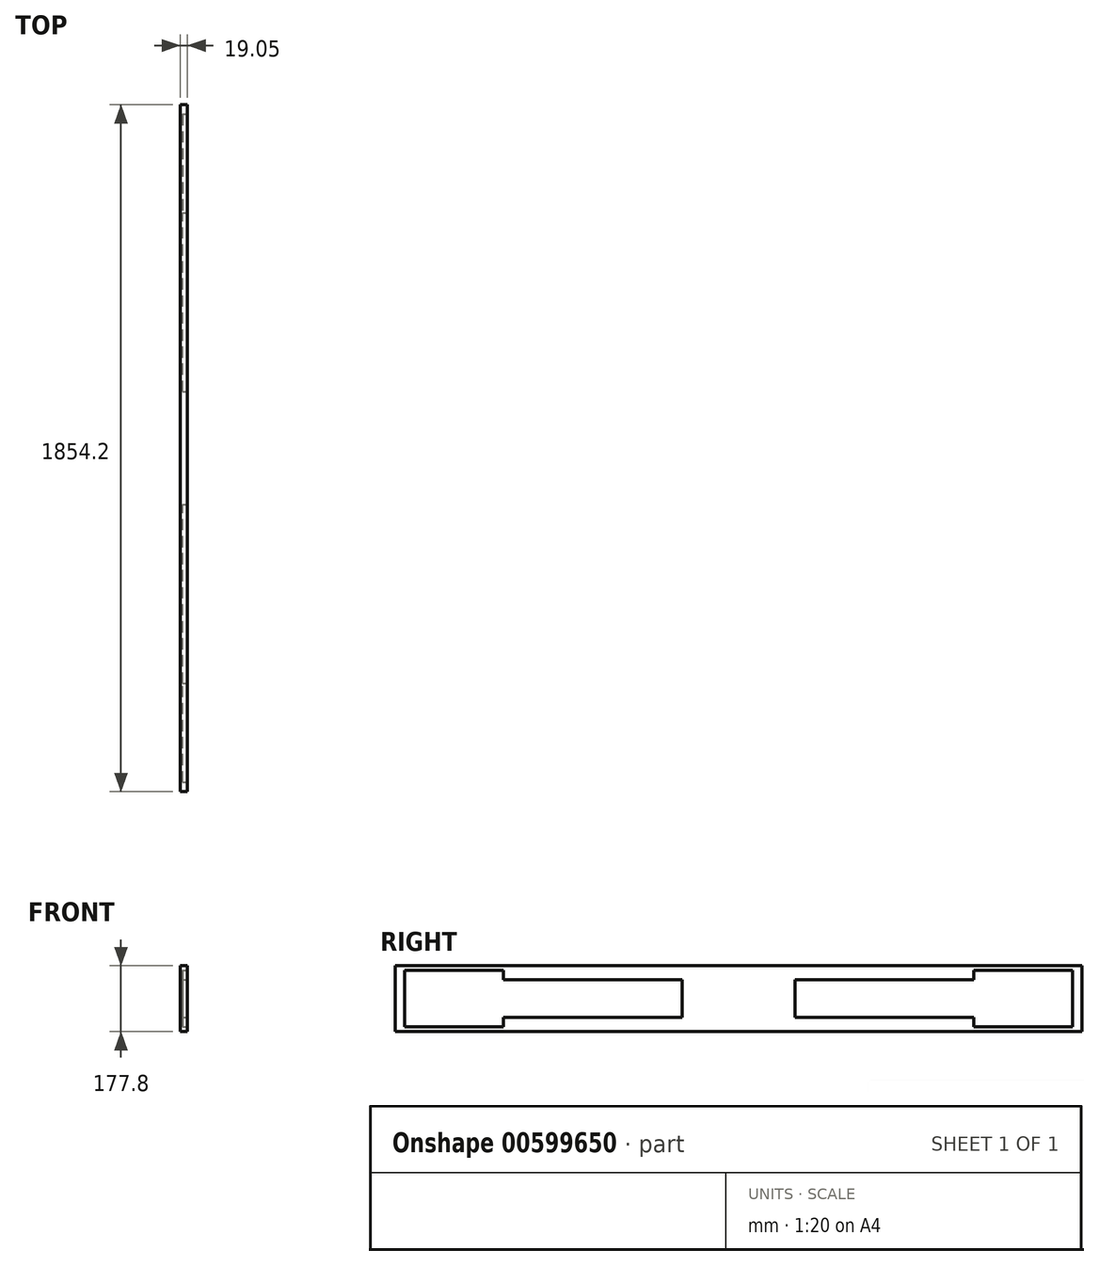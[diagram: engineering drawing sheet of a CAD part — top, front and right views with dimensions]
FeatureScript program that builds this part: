
annotation { "Feature Type Name" : "Feature", "Feature Type Description" : "" }
export const myFeature = defineFeature(function(context is Context, id is Id, definition is map)
    precondition{}
    {
        {
            var Q0;
            Q0=qCreatedBy(makeId("Front.planeOp"),FACE);
            var sketch = newSketch(context, id + "F0", { "sketchPlane" : qUnion([Q0])});
            skLineSegment(sketch, "E0.bottom", {"start": v(0, 0) * mm, "end": v(19.05, 0) * mm});
            skLineSegment(sketch, "E0.top", {"start": v(0, 177.8) * mm, "end": v(19.05, 177.8) * mm});
            skLineSegment(sketch, "E0.left", {"start": v(0, 0) * mm, "end": v(0, 177.8) * mm});
            skLineSegment(sketch, "E0.right", {"start": v(19.05, 0) * mm, "end": v(19.05, 177.8) * mm});
            skSolve(sketch);
        }
        {
            var Q0;
            Q0 = qSketchRegion(id + "F0", true);
            extrude(context, id + "F1", {"entities" : qUnion([Q0]), "endBound" : BoundingType.SYMMETRIC, "depth" : 1854.2 * mm, "offsetDistance" : 25.4 * mm});
        }
        {
            var Q0;
            Q0=makeQuery(id+"F1.opExtrude","SWEPT_FACE",FACE,{"disambiguationData":[OSD([sQuery(id+"F0.wireOp",EDGE,"E0.right")])]});
            var sketch = newSketch(context, id + "F2", { "sketchPlane" : qUnion([Q0])});
            skLineSegment(sketch, "E1", {"start": v(0, 0) * mm, "end": v(0, 177.8) * mm, "construction": true});
            skLineSegment(sketch, "E2.bottom", {"start": v(-901.7, 12.7) * mm, "end": v(-635, 12.7) * mm});
            skLineSegment(sketch, "E2.top", {"start": v(-901.7, 165.1) * mm, "end": v(-635, 165.1) * mm});
            skLineSegment(sketch, "E2.right", {"start": v(-635, 12.7) * mm, "end": v(-635, 38.1) * mm});
            skLineSegment(sketch, "E3", {"start": v(-901.7, 165.1) * mm, "end": v(-901.7, 12.7) * mm});
            skLineSegment(sketch, "E4.MirrorCS", {"start": v(901.7, 165.1) * mm, "end": v(635, 165.1) * mm});
            skLineSegment(sketch, "E5.MirrorCS", {"start": v(901.7, 12.7) * mm, "end": v(635, 12.7) * mm});
            skLineSegment(sketch, "E6.MirrorCS", {"start": v(901.7, 165.1) * mm, "end": v(901.7, 12.7) * mm});
            skLineSegment(sketch, "E7", {"start": v(-635, 139.7) * mm, "end": v(-152.4, 139.7) * mm});
            skLineSegment(sketch, "E8", {"start": v(-635, 38.1) * mm, "end": v(-152.4, 38.1) * mm});
            skLineSegment(sketch, "E9.trimOffspring", {"start": v(-635, 139.7) * mm, "end": v(-635, 165.1) * mm});
            skLineSegment(sketch, "E10.trimOffspring", {"start": v(635, 139.7) * mm, "end": v(635, 165.1) * mm});
            skLineSegment(sketch, "E11", {"start": v(635, 38.1) * mm, "end": v(635, 12.7) * mm});
            skLineSegment(sketch, "E12", {"start": v(-152.4, 139.7) * mm, "end": v(-152.4, 38.1) * mm});
            skLineSegment(sketch, "E13.MirrorCS", {"start": v(152.4, 139.7) * mm, "end": v(152.4, 38.1) * mm});
            skLineSegment(sketch, "E14.trimOffspring", {"start": v(152.4, 139.7) * mm, "end": v(635, 139.7) * mm});
            skLineSegment(sketch, "E15.trimOffspring", {"start": v(152.4, 38.1) * mm, "end": v(635, 38.1) * mm});
            skSolve(sketch);
        }
        {
            var Q0;
            Q0 = qSketchRegion(id + "F2", true);
            extrude(context, id + "F3", {"entities" : qUnion([Q0]), "operationType" : NewBodyOperationType.REMOVE, "oppositeDirection" : true, "depth" : 12.7 * mm, "offsetDistance" : 25.4 * mm});
        }
    });
